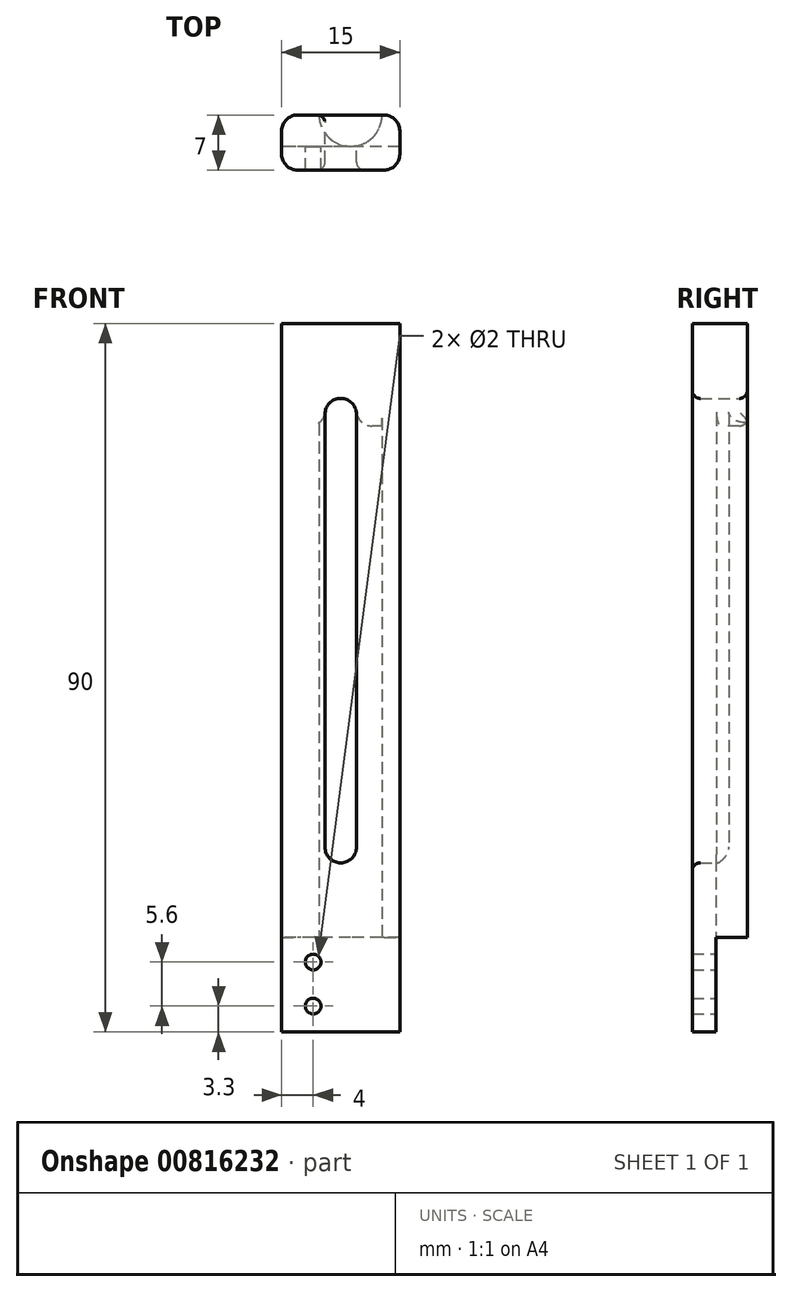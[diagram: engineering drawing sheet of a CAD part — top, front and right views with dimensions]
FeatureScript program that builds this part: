
annotation { "Feature Type Name" : "Feature", "Feature Type Description" : "" }
export const myFeature = defineFeature(function(context is Context, id is Id, definition is map)
    precondition{}
    {
        {
            var Q0;
            Q0=qCreatedBy(makeId("Top.planeOp"),FACE);
            var sketch = newSketch(context, id + "F0", { "sketchPlane" : qUnion([Q0])});
            skLineSegment(sketch, "E0.bottom", {"start": v(7.5, -3.5) * mm, "end": v(-7.5, -3.5) * mm});
            skLineSegment(sketch, "E0.top", {"start": v(7.5, 3.5) * mm, "end": v(-7.5, 3.5) * mm});
            skLineSegment(sketch, "E0.left", {"start": v(7.5, -3.5) * mm, "end": v(7.5, 3.5) * mm});
            skLineSegment(sketch, "E0.right", {"start": v(-7.5, -3.5) * mm, "end": v(-7.5, 3.5) * mm});
            skPoint(sketch, "E0.middle", {"position": v(0, 0) * mm});
            skSolve(sketch);
        }
        {
            var Q0;
            Q0=makeQuery(id+"F0.imprint","IMPRINT",FACE,{"disambiguationData":[TD([[makeQuery(id+"F0.imprint","IMPRINT",EDGE,{"derivedFrom":sQuery(id+"F0.wireOp",EDGE,"E0.bottom")}),-1.0]])]});
            extrude(context, id + "F1", {"entities" : qUnion([Q0]), "depth" : 90 * mm, "offsetDistance" : 25 * mm});
        }
        {
            var Q0;
            Q0=makeQuery(id+"F1.opExtrude","SWEPT_FACE",FACE,{"disambiguationData":[OSD([sQuery(id+"F0.wireOp",EDGE,"E0.right")])]});
            var sketch = newSketch(context, id + "F2", { "sketchPlane" : qUnion([Q0])});
            skLineSegment(sketch, "E1.bottom", {"start": v(-3.5, 0) * mm, "end": v(0.5, 0) * mm});
            skLineSegment(sketch, "E1.top", {"start": v(-3.5, 12) * mm, "end": v(0.5, 12) * mm});
            skLineSegment(sketch, "E1.left", {"start": v(-3.5, 0) * mm, "end": v(-3.5, 12) * mm});
            skLineSegment(sketch, "E1.right", {"start": v(0.5, 0) * mm, "end": v(0.5, 12) * mm});
            skSolve(sketch);
        }
        {
            var Q0;
            Q0=makeQuery(id+"F2.imprint","IMPRINT",FACE,{"disambiguationData":[TD([[makeQuery(id+"F2.imprint","IMPRINT",EDGE,{"derivedFrom":sQuery(id+"F2.wireOp",EDGE,"E1.bottom")}),-1.0]])]});
            extrude(context, id + "F3", {"entities" : qUnion([Q0]), "operationType" : NewBodyOperationType.REMOVE, "oppositeDirection" : true, "depth" : 25 * mm, "offsetDistance" : 25 * mm});
        }
        {
            var Q0;
            Q0=makeQuery(id+"F3.boolean.opBoolean","COPY",FACE,{"derivedFrom":makeQuery(id+"F3.opExtrude","SWEPT_FACE",FACE,{"disambiguationData":[OSD([sQuery(id+"F2.wireOp",EDGE,"E1.right")])]})});
            var sketch = newSketch(context, id + "F4", { "sketchPlane" : qUnion([Q0])});
            skLineSegment(sketch, "E2", {"start": v(3.5, 12) * mm, "end": v(3.5, 0) * mm, "construction": true});
            skPoint(sketch, "E3", {"position": v(3.5, 8.9) * mm});
            skPoint(sketch, "E4", {"position": v(3.5, 3.3) * mm});
            skSolve(sketch);
        }
        {
            var Q0;
            Q0=sQuery(id+"F4.wireOp",VERTEX,"E3");
            var Q1;
            Q1=sQuery(id+"F4.wireOp",VERTEX,"E4");
            var Q2;
            Q2=makeQuery(id+"F1.opExtrude","SWEPT_BODY",BODY,{"disambiguationData":[OSD([sQuery(id+"F0.wireOp",EDGE,"E0.bottom"),sQuery(id+"F0.wireOp",EDGE,"E0.top"),sQuery(id+"F0.wireOp",EDGE,"E0.left"),sQuery(id+"F0.wireOp",EDGE,"E0.right")])]});
            hole(context, id + "F5", {"style" : HoleStyle.SIMPLE, "endStyle" : HoleEndStyle.BLIND, "holeDiameter" : 2 * mm, "majorDiameter" : 5 * mm, "holeDepth" : 5 * mm, "isTappedThrough" : true, "tappedDepth" : 12 * mm, "tapClearance" : 3, "locations" : qUnion([Q0, Q1]), "scope" : qUnion([Q2])});
        }
        {
            var Q0;
            Q0=makeQuery(id+"F1.opExtrude","SWEPT_FACE",FACE,{"disambiguationData":[OSD([sQuery(id+"F0.wireOp",EDGE,"E0.top")])]});
            var sketch = newSketch(context, id + "F6", { "sketchPlane" : qUnion([Q0])});
            skLineSegment(sketch, "E5", {"start": v(0, 12) * mm, "end": v(0, 90) * mm, "construction": true});
            skPoint(sketch, "E6", {"position": v(0, 51) * mm});
            skLineSegment(sketch, "E7.bottom", {"start": v(2, 23.5) * mm, "end": v(-2, 23.5) * mm});
            skLineSegment(sketch, "E7.top", {"start": v(2, 78.5) * mm, "end": v(-2, 78.5) * mm});
            skLineSegment(sketch, "E7.left", {"start": v(2, 23.5) * mm, "end": v(2, 78.5) * mm});
            skLineSegment(sketch, "E7.right", {"start": v(-2, 23.5) * mm, "end": v(-2, 78.5) * mm});
            skCircle(sketch, "E8", {"center": v(0, 78.5) * mm, "radius": 2 * mm});
            skCircle(sketch, "E9", {"center": v(0, 23.5) * mm, "radius": 2 * mm});
            skSolve(sketch);
        }
        {
            var Q0;
            {var subQ0=sQuery(id+"F6.wireOp",EDGE,"E7.top");Q0=makeQuery(id+"F6.imprint","IMPRINT",FACE,{"disambiguationData":[TD([[makeQuery(id+"F6.imprint","IMPRINT",EDGE,{"derivedFrom":subQ0}),-1.0]])]});}
            var Q1;
            {var subQ0=sQuery(id+"F6.wireOp",EDGE,"E7.top");Q1=makeQuery(id+"F6.imprint","IMPRINT",FACE,{"disambiguationData":[TD([[makeQuery(id+"F6.imprint","IMPRINT",EDGE,{"derivedFrom":subQ0}),1.0]])]});}
            var Q2;
            {var subQ0=sQuery(id+"F6.wireOp",EDGE,"E7.left");Q2=makeQuery(id+"F6.imprint","IMPRINT",FACE,{"disambiguationData":[TD([[makeQuery(id+"F6.imprint","IMPRINT",EDGE,{"derivedFrom":subQ0}),1.0]])]});}
            var Q3;
            {var subQ0=sQuery(id+"F6.wireOp",EDGE,"E7.bottom");Q3=makeQuery(id+"F6.imprint","IMPRINT",FACE,{"disambiguationData":[TD([[makeQuery(id+"F6.imprint","IMPRINT",EDGE,{"derivedFrom":subQ0}),-1.0]])]});}
            var Q4;
            {var subQ0=sQuery(id+"F6.wireOp",EDGE,"E7.bottom");Q4=makeQuery(id+"F6.imprint","IMPRINT",FACE,{"disambiguationData":[TD([[makeQuery(id+"F6.imprint","IMPRINT",EDGE,{"derivedFrom":subQ0}),1.0]])]});}
            extrude(context, id + "F7", {"entities" : qUnion([Q0, Q1, Q2, Q3, Q4]), "operationType" : NewBodyOperationType.REMOVE, "oppositeDirection" : true, "depth" : 25 * mm, "offsetDistance" : 25 * mm});
        }
        {
            var Q0;
            Q0=makeQuery(id+"F3.boolean.opBoolean","COPY",FACE,{"derivedFrom":makeQuery(id+"F3.opExtrude","SWEPT_FACE",FACE,{"disambiguationData":[OSD([sQuery(id+"F2.wireOp",EDGE,"E1.top")])]})});
            var sketch = newSketch(context, id + "F8", { "sketchPlane" : qUnion([Q0])});
            skCircle(sketch, "E10", {"center": v(1.25, -3.5) * mm, "radius": 4 * mm});
            skSolve(sketch);
        }
        {
            var Q0;
            {var subQ0=sQuery(id+"F8.wireOp",EDGE,"E10");var subQ1=sQuery(id+"F2.wireOp",EDGE,"E1.top");var subQ2=makeQuery(id+"F8.imprint","INTERSECT",VERTEX,{"derivedFrom":[makeQuery(id+"F3.boolean.opBoolean","COPY",EDGE,{"derivedFrom":makeQuery(id+"F3.opExtrude","SWEPT_EDGE",EDGE,{"disambiguationData":[OSD([subQ1,sQuery(id+"F2.wireOp",EDGE,"E1.right")])]})}),subQ0]});Q0=makeQuery(id+"F8.imprint","IMPRINT",FACE,{"disambiguationData":[TD([[makeQuery(id+"F8.imprint","IMPRINT",EDGE,{"disambiguationData":[TD([[subQ2,1.0]])],"derivedFrom":subQ0}),1.0]])]});}
            extrude(context, id + "F9", {"entities" : qUnion([Q0]), "operationType" : NewBodyOperationType.REMOVE, "oppositeDirection" : true, "depth" : 65 * mm, "offsetDistance" : 25 * mm});
        }
        {
            var Q0;
            Q0=makeQuery(id+"F7.boolean.opBoolean","INTERSECT",EDGE,{"derivedFrom":[makeQuery(id+"F1.opExtrude","SWEPT_FACE",FACE,{"disambiguationData":[OSD([sQuery(id+"F0.wireOp",EDGE,"E0.bottom")])]}),makeQuery(id+"F7.opExtrude","SWEPT_FACE",FACE,{"disambiguationData":[OSD([sQuery(id+"F6.wireOp",EDGE,"E7.right")])]})]});
            var Q1;
            Q1=makeQuery(id+"F7.boolean.opBoolean","INTERSECT",EDGE,{"derivedFrom":[makeQuery(id+"F1.opExtrude","SWEPT_FACE",FACE,{"disambiguationData":[OSD([sQuery(id+"F0.wireOp",EDGE,"E0.bottom")])]}),makeQuery(id+"F7.opExtrude","SWEPT_FACE",FACE,{"disambiguationData":[OSD([sQuery(id+"F6.wireOp",EDGE,"E9")])]})]});
            var Q2;
            Q2=makeQuery(id+"F7.boolean.opBoolean","INTERSECT",EDGE,{"derivedFrom":[makeQuery(id+"F1.opExtrude","SWEPT_FACE",FACE,{"disambiguationData":[OSD([sQuery(id+"F0.wireOp",EDGE,"E0.bottom")])]}),makeQuery(id+"F7.opExtrude","SWEPT_FACE",FACE,{"disambiguationData":[OSD([sQuery(id+"F6.wireOp",EDGE,"E7.left")])]})]});
            var Q3;
            Q3=makeQuery(id+"F7.boolean.opBoolean","INTERSECT",EDGE,{"derivedFrom":[makeQuery(id+"F1.opExtrude","SWEPT_FACE",FACE,{"disambiguationData":[OSD([sQuery(id+"F0.wireOp",EDGE,"E0.bottom")])]}),makeQuery(id+"F7.opExtrude","SWEPT_FACE",FACE,{"disambiguationData":[OSD([sQuery(id+"F6.wireOp",EDGE,"E8")])]})]});
            fillet(context, id + "F10", {"entities" : qUnion([Q0, Q1, Q2, Q3]), "radius" : 1 * mm, "tangentPropagation" : true, "allowEdgeOverflow" : false});
        }
        {
            var Q0;
            Q0=makeQuery(id+"F9.boolean.opBoolean","INTERSECT",EDGE,{"derivedFrom":[makeQuery(id+"F7.boolean.opBoolean","COPY",FACE,{"derivedFrom":makeQuery(id+"F7.opExtrude","SWEPT_FACE",FACE,{"disambiguationData":[OSD([sQuery(id+"F6.wireOp",EDGE,"E7.right")])]})}),makeQuery(id+"F9.opExtrude","CAP_FACE",FACE,{"disambiguationData":[OSD([sQuery(id+"F0.wireOp",EDGE,"E0.top"),sQuery(id+"F0.wireOp",EDGE,"E0.right"),sQuery(id+"F2.wireOp",EDGE,"E1.top"),sQuery(id+"F2.wireOp",EDGE,"E1.left"),sQuery(id+"F8.wireOp",EDGE,"E10")])],"isStart":false})]});
            var Q1;
            Q1=makeQuery(id+"F9.boolean.opBoolean","INTERSECT",EDGE,{"derivedFrom":[makeQuery(id+"F7.boolean.opBoolean","COPY",FACE,{"derivedFrom":makeQuery(id+"F7.opExtrude","SWEPT_FACE",FACE,{"disambiguationData":[OSD([sQuery(id+"F6.wireOp",EDGE,"E7.left")])]})}),makeQuery(id+"F9.opExtrude","CAP_FACE",FACE,{"disambiguationData":[OSD([sQuery(id+"F0.wireOp",EDGE,"E0.top"),sQuery(id+"F0.wireOp",EDGE,"E0.right"),sQuery(id+"F2.wireOp",EDGE,"E1.top"),sQuery(id+"F2.wireOp",EDGE,"E1.left"),sQuery(id+"F8.wireOp",EDGE,"E10")])],"isStart":false})]});
            fillet(context, id + "F11", {"entities" : qUnion([Q0, Q1]), "radius" : 2 * mm, "tangentPropagation" : true, "allowEdgeOverflow" : false});
        }
        {
            var Q0;
            Q0=makeQuery(id+"F1.opExtrude","SWEPT_EDGE",EDGE,{"disambiguationData":[OSD([sQuery(id+"F0.wireOp",EDGE,"E0.bottom"),sQuery(id+"F0.wireOp",EDGE,"E0.right")])]});
            var Q1;
            Q1=makeQuery(id+"F1.opExtrude","SWEPT_EDGE",EDGE,{"disambiguationData":[OSD([sQuery(id+"F0.wireOp",EDGE,"E0.top"),sQuery(id+"F0.wireOp",EDGE,"E0.right")])]});
            var Q2;
            Q2=makeQuery(id+"F1.opExtrude","SWEPT_EDGE",EDGE,{"disambiguationData":[OSD([sQuery(id+"F0.wireOp",EDGE,"E0.bottom"),sQuery(id+"F0.wireOp",EDGE,"E0.left")])]});
            var Q3;
            Q3=makeQuery(id+"F1.opExtrude","SWEPT_EDGE",EDGE,{"disambiguationData":[OSD([sQuery(id+"F0.wireOp",EDGE,"E0.top"),sQuery(id+"F0.wireOp",EDGE,"E0.left")])]});
            fillet(context, id + "F12", {"entities" : qUnion([Q0, Q1, Q2, Q3]), "radius" : 2 * mm, "tangentPropagation" : true, "allowEdgeOverflow" : false});
        }
        {
            var Q0;
            {var subQ0=sQuery(id+"F8.wireOp",EDGE,"E10");var subQ1=sQuery(id+"F2.wireOp",EDGE,"E1.left");var subQ2=sQuery(id+"F2.wireOp",EDGE,"E1.top");var subQ3=sQuery(id+"F0.wireOp",EDGE,"E0.right");var subQ4=sQuery(id+"F0.wireOp",EDGE,"E0.top");Q0=makeQuery(id+"F9.boolean.opBoolean","COPY",EDGE,{"derivedFrom":makeQuery(id+"F9.opExtrude","SWEPT_EDGE",EDGE,{"disambiguationData":[OSD([subQ4,subQ3,subQ2,subQ1,subQ0]),TDD([makeQuery(id+"F8.imprint","INTERSECT",VERTEX,{"disambiguationData":[OD(1.0)],"derivedFrom":[makeQuery(id+"F3.boolean.opBoolean","COPY",EDGE,{"derivedFrom":makeQuery(id+"F3.opExtrude","SWEPT_EDGE",EDGE,{"disambiguationData":[OSD([subQ4,subQ3,subQ2,subQ1])]})}),subQ0]})])]})});}
            var Q1;
            {var subQ0=sQuery(id+"F0.wireOp",EDGE,"E0.top");Q1=makeQuery(id+"F11.opFillet","BLEND_EDGE",EDGE,{"blendedFrom":[makeQuery(id+"F9.boolean.opBoolean","INTERSECT",EDGE,{"derivedFrom":[makeQuery(id+"F7.boolean.opBoolean","COPY",FACE,{"derivedFrom":makeQuery(id+"F7.opExtrude","SWEPT_FACE",FACE,{"disambiguationData":[OSD([sQuery(id+"F6.wireOp",EDGE,"E7.left")])]})}),makeQuery(id+"F9.opExtrude","CAP_FACE",FACE,{"disambiguationData":[OSD([subQ0,sQuery(id+"F0.wireOp",EDGE,"E0.right"),sQuery(id+"F2.wireOp",EDGE,"E1.top"),sQuery(id+"F2.wireOp",EDGE,"E1.left"),sQuery(id+"F8.wireOp",EDGE,"E10")])],"isStart":false})]}),makeQuery(id+"F1.opExtrude","SWEPT_FACE",FACE,{"disambiguationData":[OSD([subQ0])]})],"blendedInto":[makeQuery(id+"F1.opExtrude","SWEPT_FACE",FACE,{"disambiguationData":[OSD([subQ0])]})]});}
            var Q2;
            Q2=makeQuery(id+"F7.boolean.opBoolean","COPY",EDGE,{"derivedFrom":makeQuery(id+"F7.opExtrude","CAP_EDGE",EDGE,{"disambiguationData":[OSD([sQuery(id+"F6.wireOp",EDGE,"E8")])],"isStart":true})});
            var Q3;
            {var subQ0=sQuery(id+"F0.wireOp",EDGE,"E0.top");Q3=makeQuery(id+"F11.opFillet","BLEND_EDGE",EDGE,{"blendedFrom":[makeQuery(id+"F9.boolean.opBoolean","INTERSECT",EDGE,{"derivedFrom":[makeQuery(id+"F7.boolean.opBoolean","COPY",FACE,{"derivedFrom":makeQuery(id+"F7.opExtrude","SWEPT_FACE",FACE,{"disambiguationData":[OSD([sQuery(id+"F6.wireOp",EDGE,"E7.right")])]})}),makeQuery(id+"F9.opExtrude","CAP_FACE",FACE,{"disambiguationData":[OSD([subQ0,sQuery(id+"F0.wireOp",EDGE,"E0.right"),sQuery(id+"F2.wireOp",EDGE,"E1.top"),sQuery(id+"F2.wireOp",EDGE,"E1.left"),sQuery(id+"F8.wireOp",EDGE,"E10")])],"isStart":false})]}),makeQuery(id+"F1.opExtrude","SWEPT_FACE",FACE,{"disambiguationData":[OSD([subQ0])]})],"blendedInto":[makeQuery(id+"F1.opExtrude","SWEPT_FACE",FACE,{"disambiguationData":[OSD([subQ0])]})]});}
            var Q4;
            {var subQ0=sQuery(id+"F8.wireOp",EDGE,"E10");var subQ1=sQuery(id+"F2.wireOp",EDGE,"E1.left");var subQ2=sQuery(id+"F2.wireOp",EDGE,"E1.top");var subQ3=sQuery(id+"F0.wireOp",EDGE,"E0.right");var subQ4=sQuery(id+"F0.wireOp",EDGE,"E0.top");Q4=makeQuery(id+"F9.boolean.opBoolean","COPY",EDGE,{"derivedFrom":makeQuery(id+"F9.opExtrude","SWEPT_EDGE",EDGE,{"disambiguationData":[OSD([subQ4,subQ3,subQ2,subQ1,subQ0]),TDD([makeQuery(id+"F8.imprint","INTERSECT",VERTEX,{"disambiguationData":[OD(0.0)],"derivedFrom":[makeQuery(id+"F3.boolean.opBoolean","COPY",EDGE,{"derivedFrom":makeQuery(id+"F3.opExtrude","SWEPT_EDGE",EDGE,{"disambiguationData":[OSD([subQ4,subQ3,subQ2,subQ1])]})}),subQ0]})])]})});}
            fillet(context, id + "F13", {"entities" : qUnion([Q0, Q1, Q2, Q3, Q4]), "radius" : 1 * mm, "tangentPropagation" : true, "allowEdgeOverflow" : false});
        }
    });
